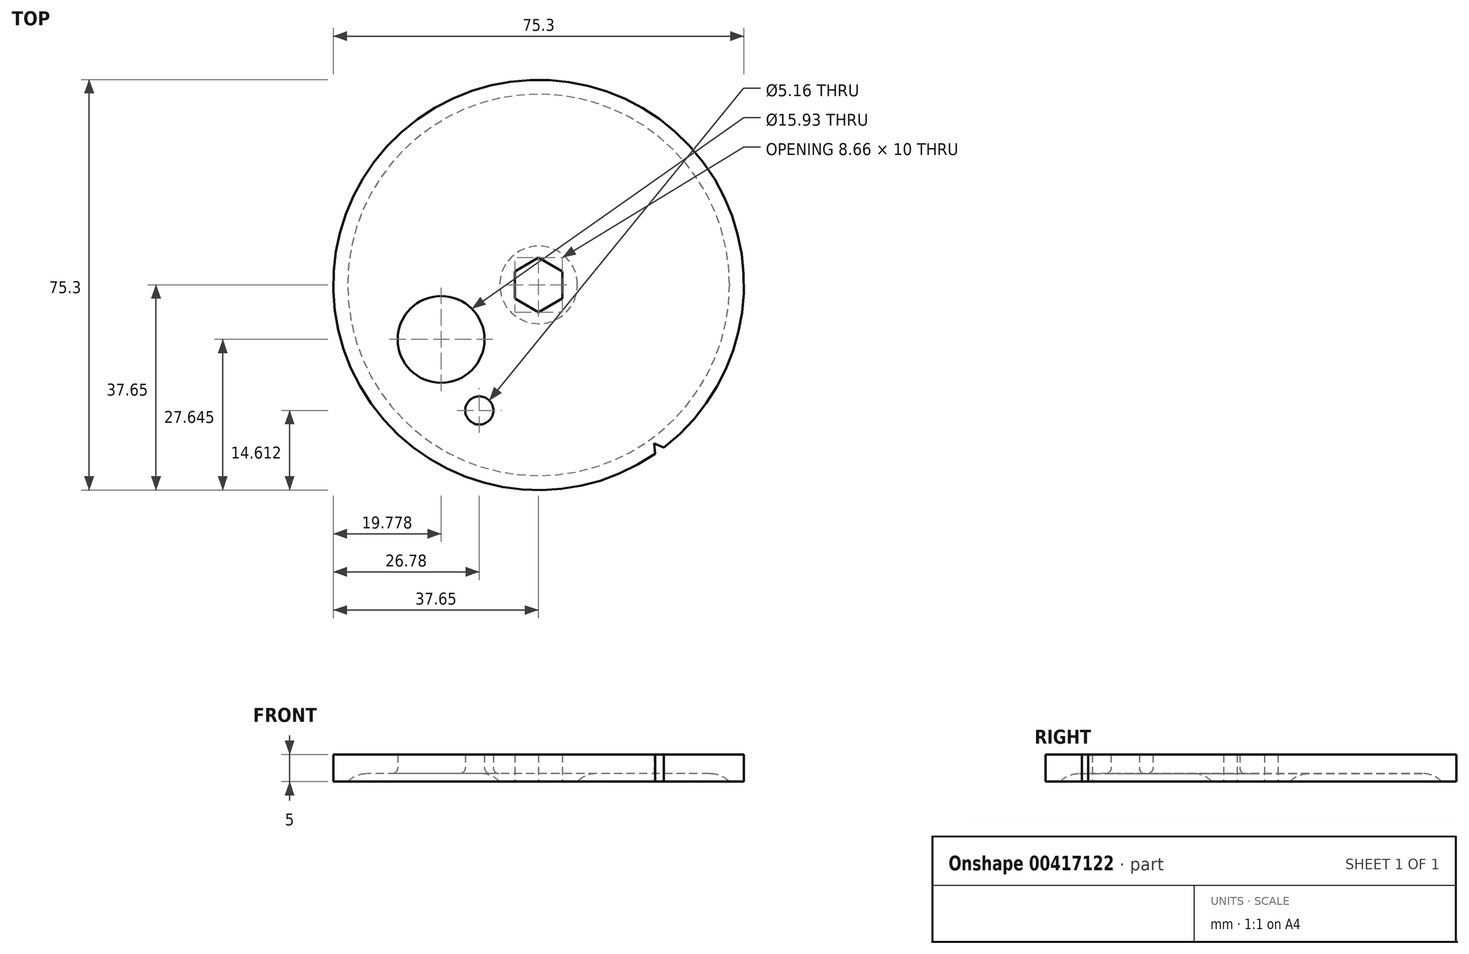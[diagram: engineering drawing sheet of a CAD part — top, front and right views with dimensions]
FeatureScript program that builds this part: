
annotation { "Feature Type Name" : "Feature", "Feature Type Description" : "" }
export const myFeature = defineFeature(function(context is Context, id is Id, definition is map)
    precondition{}
    {
        {
            var Q0;
            Q0=qCreatedBy(makeId("Top.planeOp"),FACE);
            var sketch = newSketch(context, id + "F0", { "sketchPlane" : qUnion([Q0])});
            skCircle(sketch, "E0", {"center": v(0, 0) * mm, "radius": 37.65 * mm});
            skCircle(sketch, "E1.cCircle", {"center": v(0, 0) * mm, "radius": 5 * mm, "construction": true});
            skLineSegment(sketch, "E1.0", {"start": v(0, -5) * mm, "end": v(-4.33, -2.5) * mm});
            skLineSegment(sketch, "E1.1", {"start": v(-4.33, -2.5) * mm, "end": v(-4.33, 2.5) * mm});
            skLineSegment(sketch, "E1.2", {"start": v(-4.33, 2.5) * mm, "end": v(0, 5) * mm});
            skLineSegment(sketch, "E1.3", {"start": v(0, 5) * mm, "end": v(4.33, 2.5) * mm});
            skLineSegment(sketch, "E1.4", {"start": v(4.33, 2.5) * mm, "end": v(4.33, -2.5) * mm});
            skLineSegment(sketch, "E1.5", {"start": v(4.33, -2.5) * mm, "end": v(0, -5) * mm});
            skCircle(sketch, "E2", {"center": v(0, 0) * mm, "radius": 7.12 * mm});
            skSolve(sketch);
        }
        {
            var Q0;
            Q0=makeQuery(id+"F0.imprint","IMPRINT",FACE,{"disambiguationData":[TD([[makeQuery(id+"F0.imprint","IMPRINT",EDGE,{"derivedFrom":sQuery(id+"F0.wireOp",EDGE,"E0")}),1.0]])]});
            var Q1;
            Q1=makeQuery(id+"F0.imprint","IMPRINT",FACE,{"disambiguationData":[TD([[makeQuery(id+"F0.imprint","IMPRINT",EDGE,{"derivedFrom":sQuery(id+"F0.wireOp",EDGE,"E1.0")}),1.0]])]});
            extrude(context, id + "F1", {"entities" : qUnion([Q0, Q1]), "depth" : 5 * mm});
        }
        {
            var Q0;
            Q0=qCreatedBy(makeId("Top.planeOp"),FACE);
            var sketch = newSketch(context, id + "F2", { "sketchPlane" : qUnion([Q0])});
            skCircle(sketch, "E3", {"center": v(0, 0) * mm, "radius": 38.15 * mm});
            skSolve(sketch);
        }
        {
            var Q0;
            Q0=qCreatedBy(makeId("Top.planeOp"),FACE);
            var sketch = newSketch(context, id + "F3", { "sketchPlane" : qUnion([Q0])});
            skLineSegment(sketch, "E4", {"start": v(23.47, -30.07) * mm, "end": v(21.45, -31.54) * mm});
            skLineSegment(sketch, "E5", {"start": v(21.45, -31.54) * mm, "end": v(21.19, -29.06) * mm});
            skLineSegment(sketch, "E6", {"start": v(21.19, -29.06) * mm, "end": v(23.47, -30.07) * mm});
            skSolve(sketch);
        }
        {
            var Q0;
            Q0=makeQuery(id+"F3.imprint","IMPRINT",FACE,{"disambiguationData":[TD([[makeQuery(id+"F3.imprint","IMPRINT",EDGE,{"derivedFrom":sQuery(id+"F3.wireOp",EDGE,"E4")}),-1.0]])]});
            extrude(context, id + "F4", {"entities" : qUnion([Q0]), "operationType" : NewBodyOperationType.REMOVE, "depth" : 5 * mm});
        }
        {
            var Q0;
            Q0=qCreatedBy(makeId("Front.planeOp"),FACE);
            var sketch = newSketch(context, id + "F5", { "sketchPlane" : qUnion([Q0])});
            skLineSegment(sketch, "E7", {"start": v(0, 49.92) * mm, "end": v(0, -51.95) * mm, "construction": true});
            skSolve(sketch);
        }
        {
            var Q0;
            Q0=makeQuery(id+"F0.imprint","IMPRINT",FACE,{"disambiguationData":[TD([[makeQuery(id+"F0.imprint","IMPRINT",EDGE,{"derivedFrom":sQuery(id+"F0.wireOp",EDGE,"E0")}),1.0]])]});
            var sketch = newSketch(context, id + "F6", { "sketchPlane" : qUnion([Q0])});
            skCircle(sketch, "E8", {"center": v(0, 0) * mm, "radius": 35 * mm});
            skSolve(sketch);
        }
        {
            var Q0;
            Q0=qCreatedBy(makeId("Top.planeOp"),FACE);
            cPlane(context, id + "F7", {"entities" : qUnion([Q0]), "cplaneType" : CPlaneType.OFFSET, "offset" : 2.5 * mm, "width" : 150 * mm, "height" : 150 * mm});
        }
        {
            var Q0;
            Q0=makeQuery(id+"F6.imprint","IMPRINT",FACE,{"disambiguationData":[TD([[makeQuery(id+"F6.imprint","IMPRINT",EDGE,{"derivedFrom":sQuery(id+"F6.wireOp",EDGE,"E8")}),1.0]])]});
            extrude(context, id + "F8", {"entities" : qUnion([Q0]), "operationType" : NewBodyOperationType.REMOVE, "depth" : 1.5 * mm});
        }
        {
            var Q0;
            Q0=makeQuery(id+"F8.boolean.opBoolean","COPY",EDGE,{"derivedFrom":makeQuery(id+"F8.opExtrude","CAP_EDGE",EDGE,{"disambiguationData":[OSD([sQuery(id+"F6.wireOp",EDGE,"E8")])],"isStart":false})});
            var Q1;
            Q1=makeQuery(id+"F8.boolean.opBoolean","COPY",EDGE,{"derivedFrom":makeQuery(id+"F8.opExtrude","CAP_EDGE",EDGE,{"disambiguationData":[OSD([sQuery(id+"F0.wireOp",EDGE,"E2")])],"isStart":false})});
            fillet(context, id + "F9", {"entities" : qUnion([Q0, Q1]), "radius" : 5 * mm, "tangentPropagation" : true, "allowEdgeOverflow" : false});
        }
        {
            var Q0;
            Q0=makeQuery(id+"F6.imprint","IMPRINT",FACE,{"disambiguationData":[TD([[makeQuery(id+"F6.imprint","IMPRINT",EDGE,{"derivedFrom":sQuery(id+"F6.wireOp",EDGE,"E8")}),1.0]])]});
            var sketch = newSketch(context, id + "F10", { "sketchPlane" : qUnion([Q0])});
            skCircle(sketch, "E9", {"center": v(-17.87, -10) * mm, "radius": 7.96 * mm});
            skCircle(sketch, "E10", {"center": v(-10.87, -23.04) * mm, "radius": 2.58 * mm});
            skSolve(sketch);
        }
        {
            var Q0;
            Q0 = qSketchRegion(id + "F10", true);
            extrude(context, id + "F11", {"entities" : qUnion([Q0]), "operationType" : NewBodyOperationType.REMOVE, "depth" : 10 * mm});
        }
        {
            var Q0;
            Q0=makeQuery(id+"F11.boolean.opBoolean","INTERSECT",EDGE,{"derivedFrom":[makeQuery(id+"F8.boolean.opBoolean","COPY",FACE,{"derivedFrom":makeQuery(id+"F8.opExtrude","CAP_FACE",FACE,{"disambiguationData":[OSD([sQuery(id+"F0.wireOp",EDGE,"E2"),sQuery(id+"F6.wireOp",EDGE,"E8")])],"isStart":false})}),makeQuery(id+"F11.opExtrude","SWEPT_FACE",FACE,{"disambiguationData":[OSD([sQuery(id+"F10.wireOp",EDGE,"E9")])]})]});
            var Q1;
            Q1=makeQuery(id+"F11.boolean.opBoolean","INTERSECT",EDGE,{"derivedFrom":[makeQuery(id+"F8.boolean.opBoolean","COPY",FACE,{"derivedFrom":makeQuery(id+"F8.opExtrude","CAP_FACE",FACE,{"disambiguationData":[OSD([sQuery(id+"F0.wireOp",EDGE,"E2"),sQuery(id+"F6.wireOp",EDGE,"E8")])],"isStart":false})}),makeQuery(id+"F11.opExtrude","SWEPT_FACE",FACE,{"disambiguationData":[OSD([sQuery(id+"F10.wireOp",EDGE,"E10")])]})]});
            fillet(context, id + "F12", {"entities" : qUnion([Q0, Q1]), "radius" : 1 * mm, "tangentPropagation" : true, "allowEdgeOverflow" : false});
        }
    });
